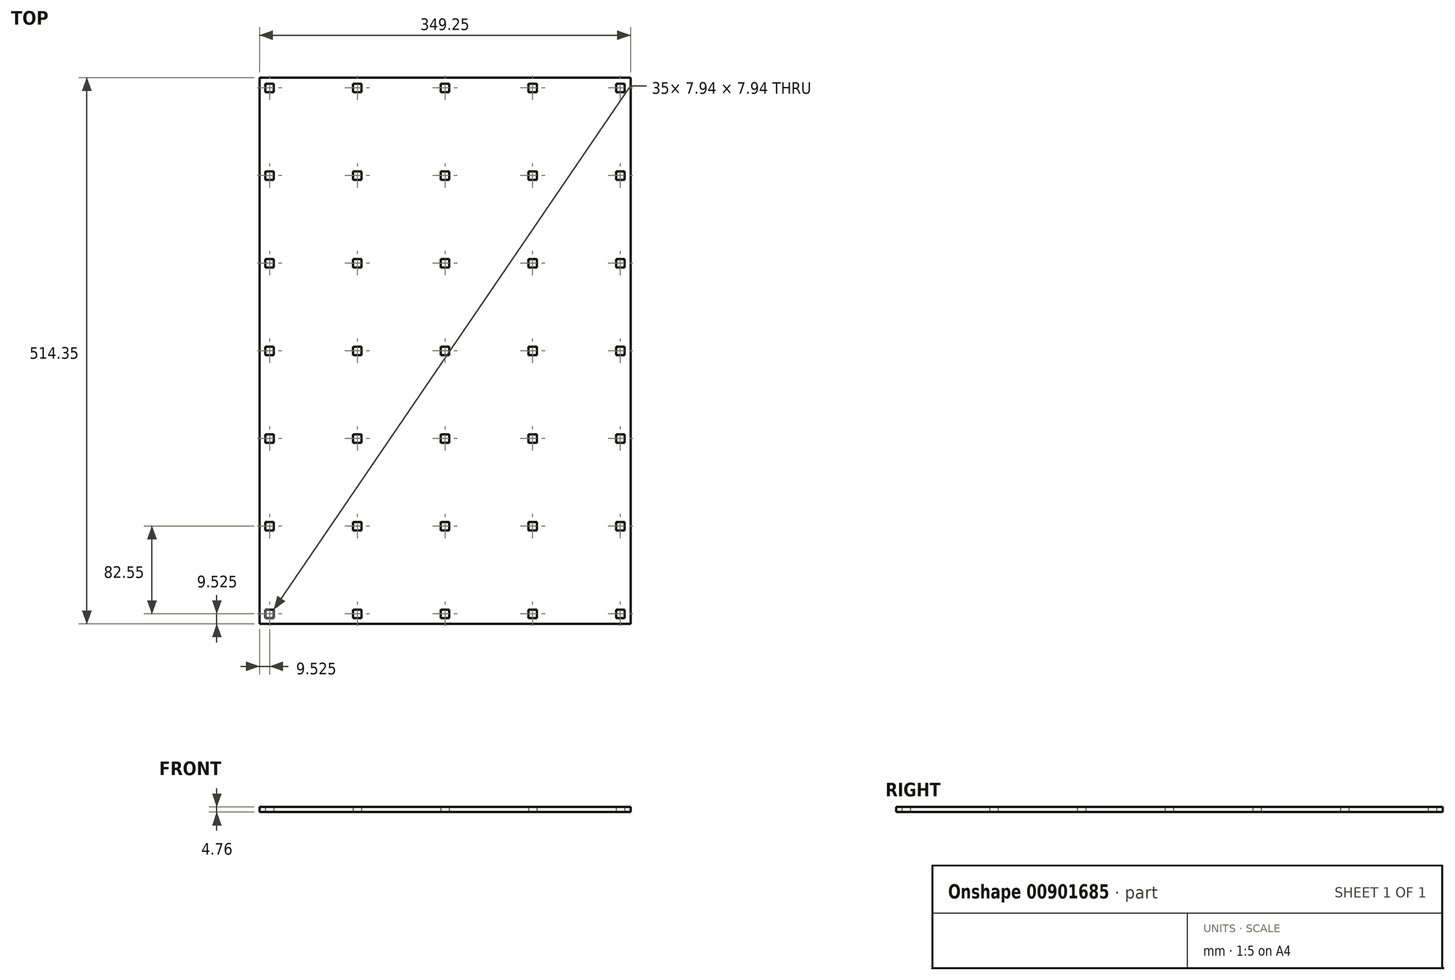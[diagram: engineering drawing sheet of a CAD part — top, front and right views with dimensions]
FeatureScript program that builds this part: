
annotation { "Feature Type Name" : "Feature", "Feature Type Description" : "" }
export const myFeature = defineFeature(function(context is Context, id is Id, definition is map)
    precondition{}
    {
        {
            var Q0;
            Q0=qCreatedBy(makeId("Top.planeOp"),FACE);
            var sketch = newSketch(context, id + "F0", { "sketchPlane" : qUnion([Q0])});
            skLineSegment(sketch, "E0.bottom", {"start": v(0, 0) * mm, "end": v(349.25, 0) * mm});
            skLineSegment(sketch, "E0.top", {"start": v(0, 514.35) * mm, "end": v(349.25, 514.35) * mm});
            skLineSegment(sketch, "E0.left", {"start": v(0, 0) * mm, "end": v(0, 514.35) * mm});
            skLineSegment(sketch, "E0.right", {"start": v(349.25, 0) * mm, "end": v(349.25, 514.35) * mm});
            skLineSegment(sketch, "E1.bottom", {"start": v(19.05, 12.7) * mm, "end": v(82.55, 12.7) * mm, "construction": true});
            skLineSegment(sketch, "E1.top", {"start": v(19.05, 88.9) * mm, "end": v(82.55, 88.9) * mm, "construction": true});
            skLineSegment(sketch, "E1.left", {"start": v(12.7, 19.05) * mm, "end": v(12.7, 82.55) * mm, "construction": true});
            skLineSegment(sketch, "E1.right", {"start": v(88.9, 19.05) * mm, "end": v(88.9, 82.55) * mm, "construction": true});
            skArc(sketch, "E2.filletArc", {"start": v(19.05, 88.9) * mm, "mid": v(14.56, 87.04) * mm, "end": v(12.7, 82.55) * mm, "construction": true});
            skArc(sketch, "E3.filletArc", {"start": v(88.9, 82.55) * mm, "mid": v(87.04, 87.04) * mm, "end": v(82.55, 88.9) * mm, "construction": true});
            skArc(sketch, "E4.filletArc", {"start": v(82.55, 12.7) * mm, "mid": v(87.04, 14.56) * mm, "end": v(88.9, 19.05) * mm, "construction": true});
            skArc(sketch, "E5.filletArc", {"start": v(12.7, 19.05) * mm, "mid": v(14.56, 14.56) * mm, "end": v(19.05, 12.7) * mm, "construction": true});
            skLineSegment(sketch, "E6.0.1.0", {"start": v(19.05, 171.45) * mm, "end": v(82.55, 171.45) * mm, "construction": true});
            skLineSegment(sketch, "E6.0.1.1", {"start": v(88.9, 101.6) * mm, "end": v(88.9, 165.1) * mm, "construction": true});
            skArc(sketch, "E6.0.1.2", {"start": v(88.9, 165.1) * mm, "mid": v(87.04, 169.6) * mm, "end": v(82.55, 171.45) * mm, "construction": true});
            skArc(sketch, "E6.0.1.3", {"start": v(82.55, 95.25) * mm, "mid": v(87.04, 97.1) * mm, "end": v(88.9, 101.6) * mm, "construction": true});
            skLineSegment(sketch, "E6.0.1.4", {"start": v(19.05, 95.25) * mm, "end": v(82.55, 95.25) * mm, "construction": true});
            skArc(sketch, "E6.0.1.5", {"start": v(12.7, 101.6) * mm, "mid": v(14.56, 97.1) * mm, "end": v(19.05, 95.25) * mm, "construction": true});
            skLineSegment(sketch, "E6.0.1.6", {"start": v(12.7, 101.6) * mm, "end": v(12.7, 165.1) * mm, "construction": true});
            skArc(sketch, "E6.0.1.7", {"start": v(19.05, 171.45) * mm, "mid": v(14.56, 169.6) * mm, "end": v(12.7, 165.1) * mm, "construction": true});
            skLineSegment(sketch, "E6.0.2.0", {"start": v(19.05, 254) * mm, "end": v(82.55, 254) * mm, "construction": true});
            skLineSegment(sketch, "E6.0.2.1", {"start": v(88.9, 184.15) * mm, "end": v(88.9, 247.65) * mm, "construction": true});
            skArc(sketch, "E6.0.2.2", {"start": v(88.9, 247.65) * mm, "mid": v(87.04, 252.14) * mm, "end": v(82.55, 254) * mm, "construction": true});
            skArc(sketch, "E6.0.2.3", {"start": v(82.55, 177.8) * mm, "mid": v(87.04, 179.66) * mm, "end": v(88.9, 184.15) * mm, "construction": true});
            skLineSegment(sketch, "E6.0.2.4", {"start": v(19.05, 177.8) * mm, "end": v(82.55, 177.8) * mm, "construction": true});
            skArc(sketch, "E6.0.2.5", {"start": v(12.7, 184.15) * mm, "mid": v(14.56, 179.66) * mm, "end": v(19.05, 177.8) * mm, "construction": true});
            skLineSegment(sketch, "E6.0.2.6", {"start": v(12.7, 184.15) * mm, "end": v(12.7, 247.65) * mm, "construction": true});
            skArc(sketch, "E6.0.2.7", {"start": v(19.05, 254) * mm, "mid": v(14.56, 252.14) * mm, "end": v(12.7, 247.65) * mm, "construction": true});
            skLineSegment(sketch, "E6.0.3.0", {"start": v(19.05, 336.55) * mm, "end": v(82.55, 336.55) * mm, "construction": true});
            skLineSegment(sketch, "E6.0.3.1", {"start": v(88.9, 266.7) * mm, "end": v(88.9, 330.2) * mm, "construction": true});
            skArc(sketch, "E6.0.3.2", {"start": v(88.9, 330.2) * mm, "mid": v(87.04, 334.7) * mm, "end": v(82.55, 336.55) * mm, "construction": true});
            skArc(sketch, "E6.0.3.3", {"start": v(82.55, 260.35) * mm, "mid": v(87.04, 262.2) * mm, "end": v(88.9, 266.7) * mm, "construction": true});
            skLineSegment(sketch, "E6.0.3.4", {"start": v(19.05, 260.35) * mm, "end": v(82.55, 260.35) * mm, "construction": true});
            skArc(sketch, "E6.0.3.5", {"start": v(12.7, 266.7) * mm, "mid": v(14.56, 262.2) * mm, "end": v(19.05, 260.35) * mm, "construction": true});
            skLineSegment(sketch, "E6.0.3.6", {"start": v(12.7, 266.7) * mm, "end": v(12.7, 330.2) * mm, "construction": true});
            skArc(sketch, "E6.0.3.7", {"start": v(19.05, 336.55) * mm, "mid": v(14.56, 334.7) * mm, "end": v(12.7, 330.2) * mm, "construction": true});
            skLineSegment(sketch, "E6.0.4.0", {"start": v(19.05, 419.1) * mm, "end": v(82.55, 419.1) * mm, "construction": true});
            skLineSegment(sketch, "E6.0.4.1", {"start": v(88.9, 349.25) * mm, "end": v(88.9, 412.75) * mm, "construction": true});
            skArc(sketch, "E6.0.4.2", {"start": v(88.9, 412.75) * mm, "mid": v(87.04, 417.24) * mm, "end": v(82.55, 419.1) * mm, "construction": true});
            skArc(sketch, "E6.0.4.3", {"start": v(82.55, 342.9) * mm, "mid": v(87.04, 344.76) * mm, "end": v(88.9, 349.25) * mm, "construction": true});
            skLineSegment(sketch, "E6.0.4.4", {"start": v(19.05, 342.9) * mm, "end": v(82.55, 342.9) * mm, "construction": true});
            skArc(sketch, "E6.0.4.5", {"start": v(12.7, 349.25) * mm, "mid": v(14.56, 344.76) * mm, "end": v(19.05, 342.9) * mm, "construction": true});
            skLineSegment(sketch, "E6.0.4.6", {"start": v(12.7, 349.25) * mm, "end": v(12.7, 412.75) * mm, "construction": true});
            skArc(sketch, "E6.0.4.7", {"start": v(19.05, 419.1) * mm, "mid": v(14.56, 417.24) * mm, "end": v(12.7, 412.75) * mm, "construction": true});
            skLineSegment(sketch, "E6.0.5.0", {"start": v(19.05, 501.65) * mm, "end": v(82.55, 501.65) * mm, "construction": true});
            skLineSegment(sketch, "E6.0.5.1", {"start": v(88.9, 431.8) * mm, "end": v(88.9, 495.3) * mm, "construction": true});
            skArc(sketch, "E6.0.5.2", {"start": v(88.9, 495.3) * mm, "mid": v(87.04, 499.8) * mm, "end": v(82.55, 501.65) * mm, "construction": true});
            skArc(sketch, "E6.0.5.3", {"start": v(82.55, 425.45) * mm, "mid": v(87.04, 427.3) * mm, "end": v(88.9, 431.8) * mm, "construction": true});
            skLineSegment(sketch, "E6.0.5.4", {"start": v(19.05, 425.45) * mm, "end": v(82.55, 425.45) * mm, "construction": true});
            skArc(sketch, "E6.0.5.5", {"start": v(12.7, 431.8) * mm, "mid": v(14.56, 427.3) * mm, "end": v(19.05, 425.45) * mm, "construction": true});
            skLineSegment(sketch, "E6.0.5.6", {"start": v(12.7, 431.8) * mm, "end": v(12.7, 495.3) * mm, "construction": true});
            skArc(sketch, "E6.0.5.7", {"start": v(19.05, 501.65) * mm, "mid": v(14.56, 499.8) * mm, "end": v(12.7, 495.3) * mm, "construction": true});
            skLineSegment(sketch, "E6.1.0.0", {"start": v(101.6, 88.9) * mm, "end": v(165.1, 88.9) * mm, "construction": true});
            skLineSegment(sketch, "E6.1.0.1", {"start": v(171.45, 19.05) * mm, "end": v(171.45, 82.55) * mm, "construction": true});
            skArc(sketch, "E6.1.0.2", {"start": v(171.45, 82.55) * mm, "mid": v(169.6, 87.04) * mm, "end": v(165.1, 88.9) * mm, "construction": true});
            skArc(sketch, "E6.1.0.3", {"start": v(165.1, 12.7) * mm, "mid": v(169.6, 14.56) * mm, "end": v(171.45, 19.05) * mm, "construction": true});
            skLineSegment(sketch, "E6.1.0.4", {"start": v(101.6, 12.7) * mm, "end": v(165.1, 12.7) * mm, "construction": true});
            skArc(sketch, "E6.1.0.5", {"start": v(95.25, 19.05) * mm, "mid": v(97.1, 14.56) * mm, "end": v(101.6, 12.7) * mm, "construction": true});
            skLineSegment(sketch, "E6.1.0.6", {"start": v(95.25, 19.05) * mm, "end": v(95.25, 82.55) * mm, "construction": true});
            skArc(sketch, "E6.1.0.7", {"start": v(101.6, 88.9) * mm, "mid": v(97.1, 87.04) * mm, "end": v(95.25, 82.55) * mm, "construction": true});
            skLineSegment(sketch, "E6.1.1.0", {"start": v(101.6, 171.45) * mm, "end": v(165.1, 171.45) * mm, "construction": true});
            skLineSegment(sketch, "E6.1.1.1", {"start": v(171.45, 101.6) * mm, "end": v(171.45, 165.1) * mm, "construction": true});
            skArc(sketch, "E6.1.1.2", {"start": v(171.45, 165.1) * mm, "mid": v(169.6, 169.6) * mm, "end": v(165.1, 171.45) * mm, "construction": true});
            skArc(sketch, "E6.1.1.3", {"start": v(165.1, 95.25) * mm, "mid": v(169.6, 97.1) * mm, "end": v(171.45, 101.6) * mm, "construction": true});
            skLineSegment(sketch, "E6.1.1.4", {"start": v(101.6, 95.25) * mm, "end": v(165.1, 95.25) * mm, "construction": true});
            skArc(sketch, "E6.1.1.5", {"start": v(95.25, 101.6) * mm, "mid": v(97.1, 97.1) * mm, "end": v(101.6, 95.25) * mm, "construction": true});
            skLineSegment(sketch, "E6.1.1.6", {"start": v(95.25, 101.6) * mm, "end": v(95.25, 165.1) * mm, "construction": true});
            skArc(sketch, "E6.1.1.7", {"start": v(101.6, 171.45) * mm, "mid": v(97.1, 169.6) * mm, "end": v(95.25, 165.1) * mm, "construction": true});
            skLineSegment(sketch, "E6.1.2.0", {"start": v(101.6, 254) * mm, "end": v(165.1, 254) * mm, "construction": true});
            skLineSegment(sketch, "E6.1.2.1", {"start": v(171.45, 184.15) * mm, "end": v(171.45, 247.65) * mm, "construction": true});
            skArc(sketch, "E6.1.2.2", {"start": v(171.45, 247.65) * mm, "mid": v(169.6, 252.14) * mm, "end": v(165.1, 254) * mm, "construction": true});
            skArc(sketch, "E6.1.2.3", {"start": v(165.1, 177.8) * mm, "mid": v(169.6, 179.66) * mm, "end": v(171.45, 184.15) * mm, "construction": true});
            skLineSegment(sketch, "E6.1.2.4", {"start": v(101.6, 177.8) * mm, "end": v(165.1, 177.8) * mm, "construction": true});
            skArc(sketch, "E6.1.2.5", {"start": v(95.25, 184.15) * mm, "mid": v(97.1, 179.66) * mm, "end": v(101.6, 177.8) * mm, "construction": true});
            skLineSegment(sketch, "E6.1.2.6", {"start": v(95.25, 184.15) * mm, "end": v(95.25, 247.65) * mm, "construction": true});
            skArc(sketch, "E6.1.2.7", {"start": v(101.6, 254) * mm, "mid": v(97.1, 252.14) * mm, "end": v(95.25, 247.65) * mm, "construction": true});
            skLineSegment(sketch, "E6.1.3.0", {"start": v(101.6, 336.55) * mm, "end": v(165.1, 336.55) * mm, "construction": true});
            skLineSegment(sketch, "E6.1.3.1", {"start": v(171.45, 266.7) * mm, "end": v(171.45, 330.2) * mm, "construction": true});
            skArc(sketch, "E6.1.3.2", {"start": v(171.45, 330.2) * mm, "mid": v(169.6, 334.7) * mm, "end": v(165.1, 336.55) * mm, "construction": true});
            skArc(sketch, "E6.1.3.3", {"start": v(165.1, 260.35) * mm, "mid": v(169.6, 262.2) * mm, "end": v(171.45, 266.7) * mm, "construction": true});
            skLineSegment(sketch, "E6.1.3.4", {"start": v(101.6, 260.35) * mm, "end": v(165.1, 260.35) * mm, "construction": true});
            skArc(sketch, "E6.1.3.5", {"start": v(95.25, 266.7) * mm, "mid": v(97.1, 262.2) * mm, "end": v(101.6, 260.35) * mm, "construction": true});
            skLineSegment(sketch, "E6.1.3.6", {"start": v(95.25, 266.7) * mm, "end": v(95.25, 330.2) * mm, "construction": true});
            skArc(sketch, "E6.1.3.7", {"start": v(101.6, 336.55) * mm, "mid": v(97.1, 334.7) * mm, "end": v(95.25, 330.2) * mm, "construction": true});
            skLineSegment(sketch, "E6.1.4.0", {"start": v(101.6, 419.1) * mm, "end": v(165.1, 419.1) * mm, "construction": true});
            skLineSegment(sketch, "E6.1.4.1", {"start": v(171.45, 349.25) * mm, "end": v(171.45, 412.75) * mm, "construction": true});
            skArc(sketch, "E6.1.4.2", {"start": v(171.45, 412.75) * mm, "mid": v(169.6, 417.24) * mm, "end": v(165.1, 419.1) * mm, "construction": true});
            skArc(sketch, "E6.1.4.3", {"start": v(165.1, 342.9) * mm, "mid": v(169.6, 344.76) * mm, "end": v(171.45, 349.25) * mm, "construction": true});
            skLineSegment(sketch, "E6.1.4.4", {"start": v(101.6, 342.9) * mm, "end": v(165.1, 342.9) * mm, "construction": true});
            skArc(sketch, "E6.1.4.5", {"start": v(95.25, 349.25) * mm, "mid": v(97.1, 344.76) * mm, "end": v(101.6, 342.9) * mm, "construction": true});
            skLineSegment(sketch, "E6.1.4.6", {"start": v(95.25, 349.25) * mm, "end": v(95.25, 412.75) * mm, "construction": true});
            skArc(sketch, "E6.1.4.7", {"start": v(101.6, 419.1) * mm, "mid": v(97.1, 417.24) * mm, "end": v(95.25, 412.75) * mm, "construction": true});
            skLineSegment(sketch, "E6.1.5.0", {"start": v(101.6, 501.65) * mm, "end": v(165.1, 501.65) * mm, "construction": true});
            skLineSegment(sketch, "E6.1.5.1", {"start": v(171.45, 431.8) * mm, "end": v(171.45, 495.3) * mm, "construction": true});
            skArc(sketch, "E6.1.5.2", {"start": v(171.45, 495.3) * mm, "mid": v(169.6, 499.8) * mm, "end": v(165.1, 501.65) * mm, "construction": true});
            skArc(sketch, "E6.1.5.3", {"start": v(165.1, 425.45) * mm, "mid": v(169.6, 427.3) * mm, "end": v(171.45, 431.8) * mm, "construction": true});
            skLineSegment(sketch, "E6.1.5.4", {"start": v(101.6, 425.45) * mm, "end": v(165.1, 425.45) * mm, "construction": true});
            skArc(sketch, "E6.1.5.5", {"start": v(95.25, 431.8) * mm, "mid": v(97.1, 427.3) * mm, "end": v(101.6, 425.45) * mm, "construction": true});
            skLineSegment(sketch, "E6.1.5.6", {"start": v(95.25, 431.8) * mm, "end": v(95.25, 495.3) * mm, "construction": true});
            skArc(sketch, "E6.1.5.7", {"start": v(101.6, 501.65) * mm, "mid": v(97.1, 499.8) * mm, "end": v(95.25, 495.3) * mm, "construction": true});
            skLineSegment(sketch, "E6.2.0.0", {"start": v(184.15, 88.9) * mm, "end": v(247.65, 88.9) * mm, "construction": true});
            skLineSegment(sketch, "E6.2.0.1", {"start": v(254, 19.05) * mm, "end": v(254, 82.55) * mm, "construction": true});
            skArc(sketch, "E6.2.0.2", {"start": v(254, 82.55) * mm, "mid": v(252.14, 87.04) * mm, "end": v(247.65, 88.9) * mm, "construction": true});
            skArc(sketch, "E6.2.0.3", {"start": v(247.65, 12.7) * mm, "mid": v(252.14, 14.56) * mm, "end": v(254, 19.05) * mm, "construction": true});
            skLineSegment(sketch, "E6.2.0.4", {"start": v(184.15, 12.7) * mm, "end": v(247.65, 12.7) * mm, "construction": true});
            skArc(sketch, "E6.2.0.5", {"start": v(177.8, 19.05) * mm, "mid": v(179.66, 14.56) * mm, "end": v(184.15, 12.7) * mm, "construction": true});
            skLineSegment(sketch, "E6.2.0.6", {"start": v(177.8, 19.05) * mm, "end": v(177.8, 82.55) * mm, "construction": true});
            skArc(sketch, "E6.2.0.7", {"start": v(184.15, 88.9) * mm, "mid": v(179.66, 87.04) * mm, "end": v(177.8, 82.55) * mm, "construction": true});
            skLineSegment(sketch, "E6.2.1.0", {"start": v(184.15, 171.45) * mm, "end": v(247.65, 171.45) * mm, "construction": true});
            skLineSegment(sketch, "E6.2.1.1", {"start": v(254, 101.6) * mm, "end": v(254, 165.1) * mm, "construction": true});
            skArc(sketch, "E6.2.1.2", {"start": v(254, 165.1) * mm, "mid": v(252.14, 169.6) * mm, "end": v(247.65, 171.45) * mm, "construction": true});
            skArc(sketch, "E6.2.1.3", {"start": v(247.65, 95.25) * mm, "mid": v(252.14, 97.1) * mm, "end": v(254, 101.6) * mm, "construction": true});
            skLineSegment(sketch, "E6.2.1.4", {"start": v(184.15, 95.25) * mm, "end": v(247.65, 95.25) * mm, "construction": true});
            skArc(sketch, "E6.2.1.5", {"start": v(177.8, 101.6) * mm, "mid": v(179.66, 97.1) * mm, "end": v(184.15, 95.25) * mm, "construction": true});
            skLineSegment(sketch, "E6.2.1.6", {"start": v(177.8, 101.6) * mm, "end": v(177.8, 165.1) * mm, "construction": true});
            skArc(sketch, "E6.2.1.7", {"start": v(184.15, 171.45) * mm, "mid": v(179.66, 169.6) * mm, "end": v(177.8, 165.1) * mm, "construction": true});
            skLineSegment(sketch, "E6.2.2.0", {"start": v(184.15, 254) * mm, "end": v(247.65, 254) * mm, "construction": true});
            skLineSegment(sketch, "E6.2.2.1", {"start": v(254, 184.15) * mm, "end": v(254, 247.65) * mm, "construction": true});
            skArc(sketch, "E6.2.2.2", {"start": v(254, 247.65) * mm, "mid": v(252.14, 252.14) * mm, "end": v(247.65, 254) * mm, "construction": true});
            skArc(sketch, "E6.2.2.3", {"start": v(247.65, 177.8) * mm, "mid": v(252.14, 179.66) * mm, "end": v(254, 184.15) * mm, "construction": true});
            skLineSegment(sketch, "E6.2.2.4", {"start": v(184.15, 177.8) * mm, "end": v(247.65, 177.8) * mm, "construction": true});
            skArc(sketch, "E6.2.2.5", {"start": v(177.8, 184.15) * mm, "mid": v(179.66, 179.66) * mm, "end": v(184.15, 177.8) * mm, "construction": true});
            skLineSegment(sketch, "E6.2.2.6", {"start": v(177.8, 184.15) * mm, "end": v(177.8, 247.65) * mm, "construction": true});
            skArc(sketch, "E6.2.2.7", {"start": v(184.15, 254) * mm, "mid": v(179.66, 252.14) * mm, "end": v(177.8, 247.65) * mm, "construction": true});
            skLineSegment(sketch, "E6.2.3.0", {"start": v(184.15, 336.55) * mm, "end": v(247.65, 336.55) * mm, "construction": true});
            skLineSegment(sketch, "E6.2.3.1", {"start": v(254, 266.7) * mm, "end": v(254, 330.2) * mm, "construction": true});
            skArc(sketch, "E6.2.3.2", {"start": v(254, 330.2) * mm, "mid": v(252.14, 334.7) * mm, "end": v(247.65, 336.55) * mm, "construction": true});
            skArc(sketch, "E6.2.3.3", {"start": v(247.65, 260.35) * mm, "mid": v(252.14, 262.2) * mm, "end": v(254, 266.7) * mm, "construction": true});
            skLineSegment(sketch, "E6.2.3.4", {"start": v(184.15, 260.35) * mm, "end": v(247.65, 260.35) * mm, "construction": true});
            skArc(sketch, "E6.2.3.5", {"start": v(177.8, 266.7) * mm, "mid": v(179.66, 262.2) * mm, "end": v(184.15, 260.35) * mm, "construction": true});
            skLineSegment(sketch, "E6.2.3.6", {"start": v(177.8, 266.7) * mm, "end": v(177.8, 330.2) * mm, "construction": true});
            skArc(sketch, "E6.2.3.7", {"start": v(184.15, 336.55) * mm, "mid": v(179.66, 334.7) * mm, "end": v(177.8, 330.2) * mm, "construction": true});
            skLineSegment(sketch, "E6.2.4.0", {"start": v(184.15, 419.1) * mm, "end": v(247.65, 419.1) * mm, "construction": true});
            skLineSegment(sketch, "E6.2.4.1", {"start": v(254, 349.25) * mm, "end": v(254, 412.75) * mm, "construction": true});
            skArc(sketch, "E6.2.4.2", {"start": v(254, 412.75) * mm, "mid": v(252.14, 417.24) * mm, "end": v(247.65, 419.1) * mm, "construction": true});
            skArc(sketch, "E6.2.4.3", {"start": v(247.65, 342.9) * mm, "mid": v(252.14, 344.76) * mm, "end": v(254, 349.25) * mm, "construction": true});
            skLineSegment(sketch, "E6.2.4.4", {"start": v(184.15, 342.9) * mm, "end": v(247.65, 342.9) * mm, "construction": true});
            skArc(sketch, "E6.2.4.5", {"start": v(177.8, 349.25) * mm, "mid": v(179.66, 344.76) * mm, "end": v(184.15, 342.9) * mm, "construction": true});
            skLineSegment(sketch, "E6.2.4.6", {"start": v(177.8, 349.25) * mm, "end": v(177.8, 412.75) * mm, "construction": true});
            skArc(sketch, "E6.2.4.7", {"start": v(184.15, 419.1) * mm, "mid": v(179.66, 417.24) * mm, "end": v(177.8, 412.75) * mm, "construction": true});
            skLineSegment(sketch, "E6.2.5.0", {"start": v(184.15, 501.65) * mm, "end": v(247.65, 501.65) * mm, "construction": true});
            skLineSegment(sketch, "E6.2.5.1", {"start": v(254, 431.8) * mm, "end": v(254, 495.3) * mm, "construction": true});
            skArc(sketch, "E6.2.5.2", {"start": v(254, 495.3) * mm, "mid": v(252.14, 499.8) * mm, "end": v(247.65, 501.65) * mm, "construction": true});
            skArc(sketch, "E6.2.5.3", {"start": v(247.65, 425.45) * mm, "mid": v(252.14, 427.3) * mm, "end": v(254, 431.8) * mm, "construction": true});
            skLineSegment(sketch, "E6.2.5.4", {"start": v(184.15, 425.45) * mm, "end": v(247.65, 425.45) * mm, "construction": true});
            skArc(sketch, "E6.2.5.5", {"start": v(177.8, 431.8) * mm, "mid": v(179.66, 427.3) * mm, "end": v(184.15, 425.45) * mm, "construction": true});
            skLineSegment(sketch, "E6.2.5.6", {"start": v(177.8, 431.8) * mm, "end": v(177.8, 495.3) * mm, "construction": true});
            skArc(sketch, "E6.2.5.7", {"start": v(184.15, 501.65) * mm, "mid": v(179.66, 499.8) * mm, "end": v(177.8, 495.3) * mm, "construction": true});
            skLineSegment(sketch, "E6.3.0.0", {"start": v(266.7, 88.9) * mm, "end": v(330.2, 88.9) * mm, "construction": true});
            skLineSegment(sketch, "E6.3.0.1", {"start": v(336.55, 19.05) * mm, "end": v(336.55, 82.55) * mm, "construction": true});
            skArc(sketch, "E6.3.0.2", {"start": v(336.55, 82.55) * mm, "mid": v(334.7, 87.04) * mm, "end": v(330.2, 88.9) * mm, "construction": true});
            skArc(sketch, "E6.3.0.3", {"start": v(330.2, 12.7) * mm, "mid": v(334.7, 14.56) * mm, "end": v(336.55, 19.05) * mm, "construction": true});
            skLineSegment(sketch, "E6.3.0.4", {"start": v(266.7, 12.7) * mm, "end": v(330.2, 12.7) * mm, "construction": true});
            skArc(sketch, "E6.3.0.5", {"start": v(260.35, 19.05) * mm, "mid": v(262.2, 14.56) * mm, "end": v(266.7, 12.7) * mm, "construction": true});
            skLineSegment(sketch, "E6.3.0.6", {"start": v(260.35, 19.05) * mm, "end": v(260.35, 82.55) * mm, "construction": true});
            skArc(sketch, "E6.3.0.7", {"start": v(266.7, 88.9) * mm, "mid": v(262.2, 87.04) * mm, "end": v(260.35, 82.55) * mm, "construction": true});
            skLineSegment(sketch, "E6.3.1.0", {"start": v(266.7, 171.45) * mm, "end": v(330.2, 171.45) * mm, "construction": true});
            skLineSegment(sketch, "E6.3.1.1", {"start": v(336.55, 101.6) * mm, "end": v(336.55, 165.1) * mm, "construction": true});
            skArc(sketch, "E6.3.1.2", {"start": v(336.55, 165.1) * mm, "mid": v(334.7, 169.6) * mm, "end": v(330.2, 171.45) * mm, "construction": true});
            skArc(sketch, "E6.3.1.3", {"start": v(330.2, 95.25) * mm, "mid": v(334.7, 97.1) * mm, "end": v(336.55, 101.6) * mm, "construction": true});
            skLineSegment(sketch, "E6.3.1.4", {"start": v(266.7, 95.25) * mm, "end": v(330.2, 95.25) * mm, "construction": true});
            skArc(sketch, "E6.3.1.5", {"start": v(260.35, 101.6) * mm, "mid": v(262.2, 97.1) * mm, "end": v(266.7, 95.25) * mm, "construction": true});
            skLineSegment(sketch, "E6.3.1.6", {"start": v(260.35, 101.6) * mm, "end": v(260.35, 165.1) * mm, "construction": true});
            skArc(sketch, "E6.3.1.7", {"start": v(266.7, 171.45) * mm, "mid": v(262.2, 169.6) * mm, "end": v(260.35, 165.1) * mm, "construction": true});
            skLineSegment(sketch, "E6.3.2.0", {"start": v(266.7, 254) * mm, "end": v(330.2, 254) * mm, "construction": true});
            skLineSegment(sketch, "E6.3.2.1", {"start": v(336.55, 184.15) * mm, "end": v(336.55, 247.65) * mm, "construction": true});
            skArc(sketch, "E6.3.2.2", {"start": v(336.55, 247.65) * mm, "mid": v(334.7, 252.14) * mm, "end": v(330.2, 254) * mm, "construction": true});
            skArc(sketch, "E6.3.2.3", {"start": v(330.2, 177.8) * mm, "mid": v(334.7, 179.66) * mm, "end": v(336.55, 184.15) * mm, "construction": true});
            skLineSegment(sketch, "E6.3.2.4", {"start": v(266.7, 177.8) * mm, "end": v(330.2, 177.8) * mm, "construction": true});
            skArc(sketch, "E6.3.2.5", {"start": v(260.35, 184.15) * mm, "mid": v(262.2, 179.66) * mm, "end": v(266.7, 177.8) * mm, "construction": true});
            skLineSegment(sketch, "E6.3.2.6", {"start": v(260.35, 184.15) * mm, "end": v(260.35, 247.65) * mm, "construction": true});
            skArc(sketch, "E6.3.2.7", {"start": v(266.7, 254) * mm, "mid": v(262.2, 252.14) * mm, "end": v(260.35, 247.65) * mm, "construction": true});
            skLineSegment(sketch, "E6.3.3.0", {"start": v(266.7, 336.55) * mm, "end": v(330.2, 336.55) * mm, "construction": true});
            skLineSegment(sketch, "E6.3.3.1", {"start": v(336.55, 266.7) * mm, "end": v(336.55, 330.2) * mm, "construction": true});
            skArc(sketch, "E6.3.3.2", {"start": v(336.55, 330.2) * mm, "mid": v(334.7, 334.7) * mm, "end": v(330.2, 336.55) * mm, "construction": true});
            skArc(sketch, "E6.3.3.3", {"start": v(330.2, 260.35) * mm, "mid": v(334.7, 262.2) * mm, "end": v(336.55, 266.7) * mm, "construction": true});
            skLineSegment(sketch, "E6.3.3.4", {"start": v(266.7, 260.35) * mm, "end": v(330.2, 260.35) * mm, "construction": true});
            skArc(sketch, "E6.3.3.5", {"start": v(260.35, 266.7) * mm, "mid": v(262.2, 262.2) * mm, "end": v(266.7, 260.35) * mm, "construction": true});
            skLineSegment(sketch, "E6.3.3.6", {"start": v(260.35, 266.7) * mm, "end": v(260.35, 330.2) * mm, "construction": true});
            skArc(sketch, "E6.3.3.7", {"start": v(266.7, 336.55) * mm, "mid": v(262.2, 334.7) * mm, "end": v(260.35, 330.2) * mm, "construction": true});
            skLineSegment(sketch, "E6.3.4.0", {"start": v(266.7, 419.1) * mm, "end": v(330.2, 419.1) * mm, "construction": true});
            skLineSegment(sketch, "E6.3.4.1", {"start": v(336.55, 349.25) * mm, "end": v(336.55, 412.75) * mm, "construction": true});
            skArc(sketch, "E6.3.4.2", {"start": v(336.55, 412.75) * mm, "mid": v(334.7, 417.24) * mm, "end": v(330.2, 419.1) * mm, "construction": true});
            skArc(sketch, "E6.3.4.3", {"start": v(330.2, 342.9) * mm, "mid": v(334.7, 344.76) * mm, "end": v(336.55, 349.25) * mm, "construction": true});
            skLineSegment(sketch, "E6.3.4.4", {"start": v(266.7, 342.9) * mm, "end": v(330.2, 342.9) * mm, "construction": true});
            skArc(sketch, "E6.3.4.5", {"start": v(260.35, 349.25) * mm, "mid": v(262.2, 344.76) * mm, "end": v(266.7, 342.9) * mm, "construction": true});
            skLineSegment(sketch, "E6.3.4.6", {"start": v(260.35, 349.25) * mm, "end": v(260.35, 412.75) * mm, "construction": true});
            skArc(sketch, "E6.3.4.7", {"start": v(266.7, 419.1) * mm, "mid": v(262.2, 417.24) * mm, "end": v(260.35, 412.75) * mm, "construction": true});
            skLineSegment(sketch, "E6.3.5.0", {"start": v(266.7, 501.65) * mm, "end": v(330.2, 501.65) * mm, "construction": true});
            skLineSegment(sketch, "E6.3.5.1", {"start": v(336.55, 431.8) * mm, "end": v(336.55, 495.3) * mm, "construction": true});
            skArc(sketch, "E6.3.5.2", {"start": v(336.55, 495.3) * mm, "mid": v(334.7, 499.8) * mm, "end": v(330.2, 501.65) * mm, "construction": true});
            skArc(sketch, "E6.3.5.3", {"start": v(330.2, 425.45) * mm, "mid": v(334.7, 427.3) * mm, "end": v(336.55, 431.8) * mm, "construction": true});
            skLineSegment(sketch, "E6.3.5.4", {"start": v(266.7, 425.45) * mm, "end": v(330.2, 425.45) * mm, "construction": true});
            skArc(sketch, "E6.3.5.5", {"start": v(260.35, 431.8) * mm, "mid": v(262.2, 427.3) * mm, "end": v(266.7, 425.45) * mm, "construction": true});
            skLineSegment(sketch, "E6.3.5.6", {"start": v(260.35, 431.8) * mm, "end": v(260.35, 495.3) * mm, "construction": true});
            skArc(sketch, "E6.3.5.7", {"start": v(266.7, 501.65) * mm, "mid": v(262.2, 499.8) * mm, "end": v(260.35, 495.3) * mm, "construction": true});
            skLineSegment(sketch, "E6.direction1", {"start": v(19.05, 12.7) * mm, "end": v(101.6, 12.7) * mm, "construction": true});
            skLineSegment(sketch, "E6.direction2", {"start": v(19.05, 12.7) * mm, "end": v(19.05, 95.25) * mm, "construction": true});
            skLineSegment(sketch, "E7", {"start": v(165.1, 101.6) * mm, "end": v(184.15, 82.55) * mm, "construction": true});
            skLineSegment(sketch, "E8", {"start": v(266.7, 101.6) * mm, "end": v(247.65, 82.55) * mm, "construction": true});
            skLineSegment(sketch, "E9", {"start": v(247.65, 184.15) * mm, "end": v(266.7, 165.1) * mm, "construction": true});
            skLineSegment(sketch, "E10", {"start": v(184.15, 184.15) * mm, "end": v(165.1, 165.1) * mm, "construction": true});
            skLineSegment(sketch, "E11", {"start": v(174.63, 174.63) * mm, "end": v(174.63, 92.08) * mm, "construction": true});
            skLineSegment(sketch, "E12", {"start": v(174.63, 92.08) * mm, "end": v(257.18, 92.08) * mm, "construction": true});
            skCircle(sketch, "E13", {"center": v(9.53, 9.53) * mm, "radius": 3.97 * mm, "construction": true});
            skCircle(sketch, "E14.0.1.0", {"center": v(9.53, 92.08) * mm, "radius": 3.97 * mm, "construction": true});
            skCircle(sketch, "E14.0.2.0", {"center": v(9.53, 174.63) * mm, "radius": 3.97 * mm, "construction": true});
            skCircle(sketch, "E14.0.3.0", {"center": v(9.53, 257.18) * mm, "radius": 3.97 * mm, "construction": true});
            skCircle(sketch, "E14.0.4.0", {"center": v(9.53, 339.73) * mm, "radius": 3.97 * mm, "construction": true});
            skCircle(sketch, "E14.0.5.0", {"center": v(9.53, 422.28) * mm, "radius": 3.97 * mm, "construction": true});
            skCircle(sketch, "E14.0.6.0", {"center": v(9.53, 504.83) * mm, "radius": 3.97 * mm, "construction": true});
            skCircle(sketch, "E14.1.0.0", {"center": v(92.08, 9.53) * mm, "radius": 3.97 * mm, "construction": true});
            skCircle(sketch, "E14.1.1.0", {"center": v(92.08, 92.08) * mm, "radius": 3.97 * mm, "construction": true});
            skCircle(sketch, "E14.1.2.0", {"center": v(92.08, 174.63) * mm, "radius": 3.97 * mm, "construction": true});
            skCircle(sketch, "E14.1.3.0", {"center": v(92.08, 257.18) * mm, "radius": 3.97 * mm, "construction": true});
            skCircle(sketch, "E14.1.4.0", {"center": v(92.08, 339.73) * mm, "radius": 3.97 * mm, "construction": true});
            skCircle(sketch, "E14.1.5.0", {"center": v(92.08, 422.28) * mm, "radius": 3.97 * mm, "construction": true});
            skCircle(sketch, "E14.1.6.0", {"center": v(92.08, 504.83) * mm, "radius": 3.97 * mm, "construction": true});
            skCircle(sketch, "E14.2.0.0", {"center": v(174.63, 9.53) * mm, "radius": 3.97 * mm, "construction": true});
            skCircle(sketch, "E14.2.1.0", {"center": v(174.63, 92.08) * mm, "radius": 3.97 * mm, "construction": true});
            skCircle(sketch, "E14.2.2.0", {"center": v(174.63, 174.63) * mm, "radius": 3.97 * mm, "construction": true});
            skCircle(sketch, "E14.2.3.0", {"center": v(174.63, 257.18) * mm, "radius": 3.97 * mm, "construction": true});
            skCircle(sketch, "E14.2.4.0", {"center": v(174.63, 339.73) * mm, "radius": 3.97 * mm, "construction": true});
            skCircle(sketch, "E14.2.5.0", {"center": v(174.63, 422.28) * mm, "radius": 3.97 * mm, "construction": true});
            skCircle(sketch, "E14.2.6.0", {"center": v(174.63, 504.83) * mm, "radius": 3.97 * mm, "construction": true});
            skCircle(sketch, "E14.3.0.0", {"center": v(257.18, 9.53) * mm, "radius": 3.97 * mm, "construction": true});
            skCircle(sketch, "E14.3.1.0", {"center": v(257.18, 92.08) * mm, "radius": 3.97 * mm, "construction": true});
            skCircle(sketch, "E14.3.2.0", {"center": v(257.18, 174.63) * mm, "radius": 3.97 * mm, "construction": true});
            skCircle(sketch, "E14.3.3.0", {"center": v(257.18, 257.18) * mm, "radius": 3.97 * mm, "construction": true});
            skCircle(sketch, "E14.3.4.0", {"center": v(257.18, 339.73) * mm, "radius": 3.97 * mm, "construction": true});
            skCircle(sketch, "E14.3.5.0", {"center": v(257.18, 422.28) * mm, "radius": 3.97 * mm, "construction": true});
            skCircle(sketch, "E14.3.6.0", {"center": v(257.18, 504.83) * mm, "radius": 3.97 * mm, "construction": true});
            skCircle(sketch, "E14.4.0.0", {"center": v(339.73, 9.53) * mm, "radius": 3.97 * mm, "construction": true});
            skCircle(sketch, "E14.4.1.0", {"center": v(339.73, 92.08) * mm, "radius": 3.97 * mm, "construction": true});
            skCircle(sketch, "E14.4.2.0", {"center": v(339.73, 174.63) * mm, "radius": 3.97 * mm, "construction": true});
            skCircle(sketch, "E14.4.3.0", {"center": v(339.73, 257.18) * mm, "radius": 3.97 * mm, "construction": true});
            skCircle(sketch, "E14.4.4.0", {"center": v(339.73, 339.73) * mm, "radius": 3.97 * mm, "construction": true});
            skCircle(sketch, "E14.4.5.0", {"center": v(339.73, 422.28) * mm, "radius": 3.97 * mm, "construction": true});
            skCircle(sketch, "E14.4.6.0", {"center": v(339.73, 504.83) * mm, "radius": 3.97 * mm, "construction": true});
            skLineSegment(sketch, "E14.direction1", {"start": v(9.53, 9.53) * mm, "end": v(92.08, 9.53) * mm, "construction": true});
            skLineSegment(sketch, "E14.direction2", {"start": v(9.53, 9.53) * mm, "end": v(9.53, 92.08) * mm, "construction": true});
            skLineSegment(sketch, "E15.bottom", {"start": v(5.56, 5.56) * mm, "end": v(13.5, 5.56) * mm});
            skLineSegment(sketch, "E15.top", {"start": v(5.56, 13.5) * mm, "end": v(13.5, 13.5) * mm});
            skLineSegment(sketch, "E15.left", {"start": v(5.56, 5.56) * mm, "end": v(5.56, 13.5) * mm});
            skLineSegment(sketch, "E15.right", {"start": v(13.5, 5.56) * mm, "end": v(13.5, 13.5) * mm});
            skLineSegment(sketch, "E16.0.1.0", {"start": v(5.56, 96.04) * mm, "end": v(13.5, 96.04) * mm});
            skLineSegment(sketch, "E16.0.1.1", {"start": v(13.5, 88.1) * mm, "end": v(13.5, 96.04) * mm});
            skLineSegment(sketch, "E16.0.1.2", {"start": v(5.56, 88.1) * mm, "end": v(13.5, 88.1) * mm});
            skLineSegment(sketch, "E16.0.1.3", {"start": v(5.56, 88.1) * mm, "end": v(5.56, 96.04) * mm});
            skLineSegment(sketch, "E16.0.2.0", {"start": v(5.56, 178.6) * mm, "end": v(13.5, 178.6) * mm});
            skLineSegment(sketch, "E16.0.2.1", {"start": v(13.5, 170.66) * mm, "end": v(13.5, 178.6) * mm});
            skLineSegment(sketch, "E16.0.2.2", {"start": v(5.56, 170.66) * mm, "end": v(13.5, 170.66) * mm});
            skLineSegment(sketch, "E16.0.2.3", {"start": v(5.56, 170.66) * mm, "end": v(5.56, 178.6) * mm});
            skLineSegment(sketch, "E16.0.3.0", {"start": v(5.56, 261.14) * mm, "end": v(13.5, 261.14) * mm});
            skLineSegment(sketch, "E16.0.3.1", {"start": v(13.5, 253.2) * mm, "end": v(13.5, 261.14) * mm});
            skLineSegment(sketch, "E16.0.3.2", {"start": v(5.56, 253.2) * mm, "end": v(13.5, 253.2) * mm});
            skLineSegment(sketch, "E16.0.3.3", {"start": v(5.56, 253.2) * mm, "end": v(5.56, 261.14) * mm});
            skLineSegment(sketch, "E16.0.4.0", {"start": v(5.56, 343.7) * mm, "end": v(13.5, 343.7) * mm});
            skLineSegment(sketch, "E16.0.4.1", {"start": v(13.5, 335.76) * mm, "end": v(13.5, 343.7) * mm});
            skLineSegment(sketch, "E16.0.4.2", {"start": v(5.56, 335.76) * mm, "end": v(13.5, 335.76) * mm});
            skLineSegment(sketch, "E16.0.4.3", {"start": v(5.56, 335.76) * mm, "end": v(5.56, 343.7) * mm});
            skLineSegment(sketch, "E16.0.5.0", {"start": v(5.56, 426.24) * mm, "end": v(13.5, 426.24) * mm});
            skLineSegment(sketch, "E16.0.5.1", {"start": v(13.5, 418.3) * mm, "end": v(13.5, 426.24) * mm});
            skLineSegment(sketch, "E16.0.5.2", {"start": v(5.56, 418.3) * mm, "end": v(13.5, 418.3) * mm});
            skLineSegment(sketch, "E16.0.5.3", {"start": v(5.56, 418.3) * mm, "end": v(5.56, 426.24) * mm});
            skLineSegment(sketch, "E16.0.6.0", {"start": v(5.56, 508.8) * mm, "end": v(13.5, 508.8) * mm});
            skLineSegment(sketch, "E16.0.6.1", {"start": v(13.5, 500.86) * mm, "end": v(13.5, 508.8) * mm});
            skLineSegment(sketch, "E16.0.6.2", {"start": v(5.56, 500.86) * mm, "end": v(13.5, 500.86) * mm});
            skLineSegment(sketch, "E16.0.6.3", {"start": v(5.56, 500.86) * mm, "end": v(5.56, 508.8) * mm});
            skLineSegment(sketch, "E16.1.0.0", {"start": v(88.1, 13.5) * mm, "end": v(96.04, 13.5) * mm});
            skLineSegment(sketch, "E16.1.0.1", {"start": v(96.04, 5.56) * mm, "end": v(96.04, 13.5) * mm});
            skLineSegment(sketch, "E16.1.0.2", {"start": v(88.1, 5.56) * mm, "end": v(96.04, 5.56) * mm});
            skLineSegment(sketch, "E16.1.0.3", {"start": v(88.1, 5.56) * mm, "end": v(88.1, 13.5) * mm});
            skLineSegment(sketch, "E16.1.1.0", {"start": v(88.1, 96.04) * mm, "end": v(96.04, 96.04) * mm});
            skLineSegment(sketch, "E16.1.1.1", {"start": v(96.04, 88.1) * mm, "end": v(96.04, 96.04) * mm});
            skLineSegment(sketch, "E16.1.1.2", {"start": v(88.1, 88.1) * mm, "end": v(96.04, 88.1) * mm});
            skLineSegment(sketch, "E16.1.1.3", {"start": v(88.1, 88.1) * mm, "end": v(88.1, 96.04) * mm});
            skLineSegment(sketch, "E16.1.2.0", {"start": v(88.1, 178.6) * mm, "end": v(96.04, 178.6) * mm});
            skLineSegment(sketch, "E16.1.2.1", {"start": v(96.04, 170.66) * mm, "end": v(96.04, 178.6) * mm});
            skLineSegment(sketch, "E16.1.2.2", {"start": v(88.1, 170.66) * mm, "end": v(96.04, 170.66) * mm});
            skLineSegment(sketch, "E16.1.2.3", {"start": v(88.1, 170.66) * mm, "end": v(88.1, 178.6) * mm});
            skLineSegment(sketch, "E16.1.3.0", {"start": v(88.1, 261.14) * mm, "end": v(96.04, 261.14) * mm});
            skLineSegment(sketch, "E16.1.3.1", {"start": v(96.04, 253.2) * mm, "end": v(96.04, 261.14) * mm});
            skLineSegment(sketch, "E16.1.3.2", {"start": v(88.1, 253.2) * mm, "end": v(96.04, 253.2) * mm});
            skLineSegment(sketch, "E16.1.3.3", {"start": v(88.1, 253.2) * mm, "end": v(88.1, 261.14) * mm});
            skLineSegment(sketch, "E16.1.4.0", {"start": v(88.1, 343.7) * mm, "end": v(96.04, 343.7) * mm});
            skLineSegment(sketch, "E16.1.4.1", {"start": v(96.04, 335.76) * mm, "end": v(96.04, 343.7) * mm});
            skLineSegment(sketch, "E16.1.4.2", {"start": v(88.1, 335.76) * mm, "end": v(96.04, 335.76) * mm});
            skLineSegment(sketch, "E16.1.4.3", {"start": v(88.1, 335.76) * mm, "end": v(88.1, 343.7) * mm});
            skLineSegment(sketch, "E16.1.5.0", {"start": v(88.1, 426.24) * mm, "end": v(96.04, 426.24) * mm});
            skLineSegment(sketch, "E16.1.5.1", {"start": v(96.04, 418.3) * mm, "end": v(96.04, 426.24) * mm});
            skLineSegment(sketch, "E16.1.5.2", {"start": v(88.1, 418.3) * mm, "end": v(96.04, 418.3) * mm});
            skLineSegment(sketch, "E16.1.5.3", {"start": v(88.1, 418.3) * mm, "end": v(88.1, 426.24) * mm});
            skLineSegment(sketch, "E16.1.6.0", {"start": v(88.1, 508.8) * mm, "end": v(96.04, 508.8) * mm});
            skLineSegment(sketch, "E16.1.6.1", {"start": v(96.04, 500.86) * mm, "end": v(96.04, 508.8) * mm});
            skLineSegment(sketch, "E16.1.6.2", {"start": v(88.1, 500.86) * mm, "end": v(96.04, 500.86) * mm});
            skLineSegment(sketch, "E16.1.6.3", {"start": v(88.1, 500.86) * mm, "end": v(88.1, 508.8) * mm});
            skLineSegment(sketch, "E16.2.0.0", {"start": v(170.66, 13.5) * mm, "end": v(178.6, 13.5) * mm});
            skLineSegment(sketch, "E16.2.0.1", {"start": v(178.6, 5.56) * mm, "end": v(178.6, 13.5) * mm});
            skLineSegment(sketch, "E16.2.0.2", {"start": v(170.66, 5.56) * mm, "end": v(178.6, 5.56) * mm});
            skLineSegment(sketch, "E16.2.0.3", {"start": v(170.66, 5.56) * mm, "end": v(170.66, 13.5) * mm});
            skLineSegment(sketch, "E16.2.1.0", {"start": v(170.66, 96.04) * mm, "end": v(178.6, 96.04) * mm});
            skLineSegment(sketch, "E16.2.1.1", {"start": v(178.6, 88.1) * mm, "end": v(178.6, 96.04) * mm});
            skLineSegment(sketch, "E16.2.1.2", {"start": v(170.66, 88.1) * mm, "end": v(178.6, 88.1) * mm});
            skLineSegment(sketch, "E16.2.1.3", {"start": v(170.66, 88.1) * mm, "end": v(170.66, 96.04) * mm});
            skLineSegment(sketch, "E16.2.2.0", {"start": v(170.66, 178.6) * mm, "end": v(178.6, 178.6) * mm});
            skLineSegment(sketch, "E16.2.2.1", {"start": v(178.6, 170.66) * mm, "end": v(178.6, 178.6) * mm});
            skLineSegment(sketch, "E16.2.2.2", {"start": v(170.66, 170.66) * mm, "end": v(178.6, 170.66) * mm});
            skLineSegment(sketch, "E16.2.2.3", {"start": v(170.66, 170.66) * mm, "end": v(170.66, 178.6) * mm});
            skLineSegment(sketch, "E16.2.3.0", {"start": v(170.66, 261.14) * mm, "end": v(178.6, 261.14) * mm});
            skLineSegment(sketch, "E16.2.3.1", {"start": v(178.6, 253.2) * mm, "end": v(178.6, 261.14) * mm});
            skLineSegment(sketch, "E16.2.3.2", {"start": v(170.66, 253.2) * mm, "end": v(178.6, 253.2) * mm});
            skLineSegment(sketch, "E16.2.3.3", {"start": v(170.66, 253.2) * mm, "end": v(170.66, 261.14) * mm});
            skLineSegment(sketch, "E16.2.4.0", {"start": v(170.66, 343.7) * mm, "end": v(178.6, 343.7) * mm});
            skLineSegment(sketch, "E16.2.4.1", {"start": v(178.6, 335.76) * mm, "end": v(178.6, 343.7) * mm});
            skLineSegment(sketch, "E16.2.4.2", {"start": v(170.66, 335.76) * mm, "end": v(178.6, 335.76) * mm});
            skLineSegment(sketch, "E16.2.4.3", {"start": v(170.66, 335.76) * mm, "end": v(170.66, 343.7) * mm});
            skLineSegment(sketch, "E16.2.5.0", {"start": v(170.66, 426.24) * mm, "end": v(178.6, 426.24) * mm});
            skLineSegment(sketch, "E16.2.5.1", {"start": v(178.6, 418.3) * mm, "end": v(178.6, 426.24) * mm});
            skLineSegment(sketch, "E16.2.5.2", {"start": v(170.66, 418.3) * mm, "end": v(178.6, 418.3) * mm});
            skLineSegment(sketch, "E16.2.5.3", {"start": v(170.66, 418.3) * mm, "end": v(170.66, 426.24) * mm});
            skLineSegment(sketch, "E16.2.6.0", {"start": v(170.66, 508.8) * mm, "end": v(178.6, 508.8) * mm});
            skLineSegment(sketch, "E16.2.6.1", {"start": v(178.6, 500.86) * mm, "end": v(178.6, 508.8) * mm});
            skLineSegment(sketch, "E16.2.6.2", {"start": v(170.66, 500.86) * mm, "end": v(178.6, 500.86) * mm});
            skLineSegment(sketch, "E16.2.6.3", {"start": v(170.66, 500.86) * mm, "end": v(170.66, 508.8) * mm});
            skLineSegment(sketch, "E16.3.0.0", {"start": v(253.2, 13.5) * mm, "end": v(261.14, 13.5) * mm});
            skLineSegment(sketch, "E16.3.0.1", {"start": v(261.14, 5.56) * mm, "end": v(261.14, 13.5) * mm});
            skLineSegment(sketch, "E16.3.0.2", {"start": v(253.2, 5.56) * mm, "end": v(261.14, 5.56) * mm});
            skLineSegment(sketch, "E16.3.0.3", {"start": v(253.2, 5.56) * mm, "end": v(253.2, 13.5) * mm});
            skLineSegment(sketch, "E16.3.1.0", {"start": v(253.2, 96.04) * mm, "end": v(261.14, 96.04) * mm});
            skLineSegment(sketch, "E16.3.1.1", {"start": v(261.14, 88.1) * mm, "end": v(261.14, 96.04) * mm});
            skLineSegment(sketch, "E16.3.1.2", {"start": v(253.2, 88.1) * mm, "end": v(261.14, 88.1) * mm});
            skLineSegment(sketch, "E16.3.1.3", {"start": v(253.2, 88.1) * mm, "end": v(253.2, 96.04) * mm});
            skLineSegment(sketch, "E16.3.2.0", {"start": v(253.2, 178.6) * mm, "end": v(261.14, 178.6) * mm});
            skLineSegment(sketch, "E16.3.2.1", {"start": v(261.14, 170.66) * mm, "end": v(261.14, 178.6) * mm});
            skLineSegment(sketch, "E16.3.2.2", {"start": v(253.2, 170.66) * mm, "end": v(261.14, 170.66) * mm});
            skLineSegment(sketch, "E16.3.2.3", {"start": v(253.2, 170.66) * mm, "end": v(253.2, 178.6) * mm});
            skLineSegment(sketch, "E16.3.3.0", {"start": v(253.2, 261.14) * mm, "end": v(261.14, 261.14) * mm});
            skLineSegment(sketch, "E16.3.3.1", {"start": v(261.14, 253.2) * mm, "end": v(261.14, 261.14) * mm});
            skLineSegment(sketch, "E16.3.3.2", {"start": v(253.2, 253.2) * mm, "end": v(261.14, 253.2) * mm});
            skLineSegment(sketch, "E16.3.3.3", {"start": v(253.2, 253.2) * mm, "end": v(253.2, 261.14) * mm});
            skLineSegment(sketch, "E16.3.4.0", {"start": v(253.2, 343.7) * mm, "end": v(261.14, 343.7) * mm});
            skLineSegment(sketch, "E16.3.4.1", {"start": v(261.14, 335.76) * mm, "end": v(261.14, 343.7) * mm});
            skLineSegment(sketch, "E16.3.4.2", {"start": v(253.2, 335.76) * mm, "end": v(261.14, 335.76) * mm});
            skLineSegment(sketch, "E16.3.4.3", {"start": v(253.2, 335.76) * mm, "end": v(253.2, 343.7) * mm});
            skLineSegment(sketch, "E16.3.5.0", {"start": v(253.2, 426.24) * mm, "end": v(261.14, 426.24) * mm});
            skLineSegment(sketch, "E16.3.5.1", {"start": v(261.14, 418.3) * mm, "end": v(261.14, 426.24) * mm});
            skLineSegment(sketch, "E16.3.5.2", {"start": v(253.2, 418.3) * mm, "end": v(261.14, 418.3) * mm});
            skLineSegment(sketch, "E16.3.5.3", {"start": v(253.2, 418.3) * mm, "end": v(253.2, 426.24) * mm});
            skLineSegment(sketch, "E16.3.6.0", {"start": v(253.2, 508.8) * mm, "end": v(261.14, 508.8) * mm});
            skLineSegment(sketch, "E16.3.6.1", {"start": v(261.14, 500.86) * mm, "end": v(261.14, 508.8) * mm});
            skLineSegment(sketch, "E16.3.6.2", {"start": v(253.2, 500.86) * mm, "end": v(261.14, 500.86) * mm});
            skLineSegment(sketch, "E16.3.6.3", {"start": v(253.2, 500.86) * mm, "end": v(253.2, 508.8) * mm});
            skLineSegment(sketch, "E16.4.0.0", {"start": v(335.76, 13.5) * mm, "end": v(343.7, 13.5) * mm});
            skLineSegment(sketch, "E16.4.0.1", {"start": v(343.7, 5.56) * mm, "end": v(343.7, 13.5) * mm});
            skLineSegment(sketch, "E16.4.0.2", {"start": v(335.76, 5.56) * mm, "end": v(343.7, 5.56) * mm});
            skLineSegment(sketch, "E16.4.0.3", {"start": v(335.76, 5.56) * mm, "end": v(335.76, 13.5) * mm});
            skLineSegment(sketch, "E16.4.1.0", {"start": v(335.76, 96.04) * mm, "end": v(343.7, 96.04) * mm});
            skLineSegment(sketch, "E16.4.1.1", {"start": v(343.7, 88.1) * mm, "end": v(343.7, 96.04) * mm});
            skLineSegment(sketch, "E16.4.1.2", {"start": v(335.76, 88.1) * mm, "end": v(343.7, 88.1) * mm});
            skLineSegment(sketch, "E16.4.1.3", {"start": v(335.76, 88.1) * mm, "end": v(335.76, 96.04) * mm});
            skLineSegment(sketch, "E16.4.2.0", {"start": v(335.76, 178.6) * mm, "end": v(343.7, 178.6) * mm});
            skLineSegment(sketch, "E16.4.2.1", {"start": v(343.7, 170.66) * mm, "end": v(343.7, 178.6) * mm});
            skLineSegment(sketch, "E16.4.2.2", {"start": v(335.76, 170.66) * mm, "end": v(343.7, 170.66) * mm});
            skLineSegment(sketch, "E16.4.2.3", {"start": v(335.76, 170.66) * mm, "end": v(335.76, 178.6) * mm});
            skLineSegment(sketch, "E16.4.3.0", {"start": v(335.76, 261.14) * mm, "end": v(343.7, 261.14) * mm});
            skLineSegment(sketch, "E16.4.3.1", {"start": v(343.7, 253.2) * mm, "end": v(343.7, 261.14) * mm});
            skLineSegment(sketch, "E16.4.3.2", {"start": v(335.76, 253.2) * mm, "end": v(343.7, 253.2) * mm});
            skLineSegment(sketch, "E16.4.3.3", {"start": v(335.76, 253.2) * mm, "end": v(335.76, 261.14) * mm});
            skLineSegment(sketch, "E16.4.4.0", {"start": v(335.76, 343.7) * mm, "end": v(343.7, 343.7) * mm});
            skLineSegment(sketch, "E16.4.4.1", {"start": v(343.7, 335.76) * mm, "end": v(343.7, 343.7) * mm});
            skLineSegment(sketch, "E16.4.4.2", {"start": v(335.76, 335.76) * mm, "end": v(343.7, 335.76) * mm});
            skLineSegment(sketch, "E16.4.4.3", {"start": v(335.76, 335.76) * mm, "end": v(335.76, 343.7) * mm});
            skLineSegment(sketch, "E16.4.5.0", {"start": v(335.76, 426.24) * mm, "end": v(343.7, 426.24) * mm});
            skLineSegment(sketch, "E16.4.5.1", {"start": v(343.7, 418.3) * mm, "end": v(343.7, 426.24) * mm});
            skLineSegment(sketch, "E16.4.5.2", {"start": v(335.76, 418.3) * mm, "end": v(343.7, 418.3) * mm});
            skLineSegment(sketch, "E16.4.5.3", {"start": v(335.76, 418.3) * mm, "end": v(335.76, 426.24) * mm});
            skLineSegment(sketch, "E16.4.6.0", {"start": v(335.76, 508.8) * mm, "end": v(343.7, 508.8) * mm});
            skLineSegment(sketch, "E16.4.6.1", {"start": v(343.7, 500.86) * mm, "end": v(343.7, 508.8) * mm});
            skLineSegment(sketch, "E16.4.6.2", {"start": v(335.76, 500.86) * mm, "end": v(343.7, 500.86) * mm});
            skLineSegment(sketch, "E16.4.6.3", {"start": v(335.76, 500.86) * mm, "end": v(335.76, 508.8) * mm});
            skLineSegment(sketch, "E16.direction1", {"start": v(5.56, 5.56) * mm, "end": v(88.1, 5.56) * mm, "construction": true});
            skLineSegment(sketch, "E16.direction2", {"start": v(5.56, 5.56) * mm, "end": v(5.56, 88.1) * mm, "construction": true});
            skSolve(sketch);
        }
        {
            var Q0;
            Q0=makeQuery(id+"F0.imprint","IMPRINT",FACE,{"disambiguationData":[TD([[makeQuery(id+"F0.imprint","IMPRINT",EDGE,{"derivedFrom":sQuery(id+"F0.wireOp",EDGE,"E0.bottom")}),1.0]])]});
            extrude(context, id + "F1", {"entities" : qUnion([Q0]), "depth" : 4.76 * mm, "offsetDistance" : 25.4 * mm});
        }
    });
